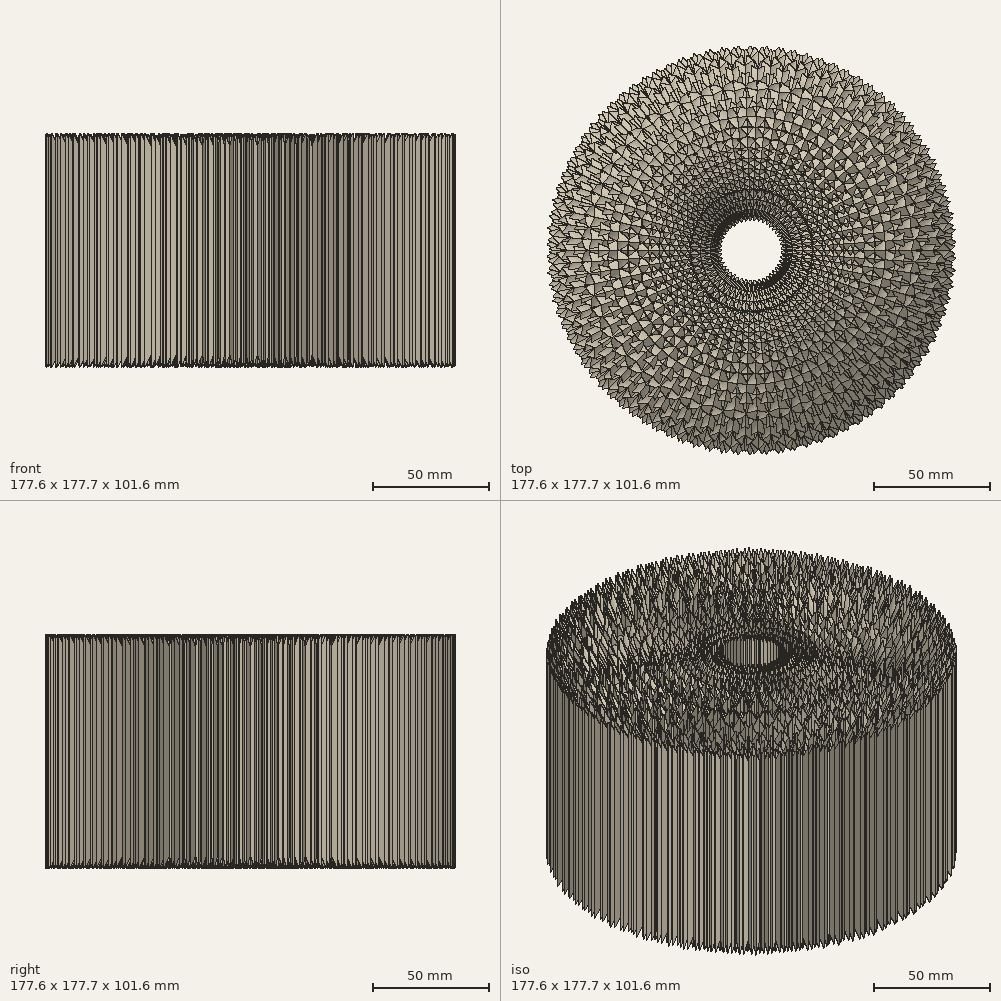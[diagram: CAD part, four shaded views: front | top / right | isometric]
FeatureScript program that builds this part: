
annotation { "Feature Type Name" : "Feature", "Feature Type Description" : "" }
export const myFeature = defineFeature(function(context is Context, id is Id, definition is map)
    precondition{}
    {
        {
            var Q0;
            Q0=qCreatedBy(makeId("Front.planeOp"),FACE);
            var sketch = newSketch(context, id + "F0", { "sketchPlane" : qUnion([Q0])});
            skLineSegment(sketch, "E0", {"start": v(0, -3.4) * mm, "end": v(0, 98.2) * mm});
            skLineSegment(sketch, "E1", {"start": v(-12.7, 0) * mm, "end": v(-12.7, 101.6) * mm});
            skArc(sketch, "E2", {"start": v(-12.7, 101.6) * mm, "mid": v(-26.31, 50.8) * mm, "end": v(-12.7, 0) * mm});
            skLineSegment(sketch, "E3", {"start": v(-50.8, 91.75) * mm, "end": v(-50.8, 14) * mm});
            skSolve(sketch);
        }
        {
            var Q0;
            Q0 = qSketchRegion(id + "F0", true);
            var Q1;
            Q1=sQuery(id+"F0.wireOp",EDGE,"E1");
            revolve(context, id + "F1", {"entities" : qUnion([Q0]), "axis" : qUnion([Q1]), "revolveType" : RevolveType.SYMMETRIC, "angle" : 60 * degree});
        }
        {
            var Q0;
            Q0=makeQuery(id+"F1.opRevolve","SWEPT_BODY",BODY,{"disambiguationData":[OSD([sQuery(id+"F0.wireOp",EDGE,"E1"),sQuery(id+"F0.wireOp",EDGE,"E2")])]});
            var Q1;
            Q1=sQuery(id+"F0.wireOp",EDGE,"E3");
            circularPattern(context, id + "F2", {"entities" : qUnion([Q0]), "axis" : qUnion([Q1]), "angle" : 360 * degree, "instanceCount" : 45, "equalSpace" : true, "computeTransformsWithoutBuiltin" : true});
        }
        {
            var Q0;
            Q0=makeQuery(id+"F2.opPattern","COPY",BODY,{"derivedFrom":makeQuery(id+"F1.opRevolve","SWEPT_BODY",BODY,{"disambiguationData":[OSD([sQuery(id+"F0.wireOp",EDGE,"E1"),sQuery(id+"F0.wireOp",EDGE,"E2")])]}),"instanceName":"5"});
            var Q1;
            Q1=makeQuery(id+"F2.opPattern","COPY",BODY,{"derivedFrom":makeQuery(id+"F1.opRevolve","SWEPT_BODY",BODY,{"disambiguationData":[OSD([sQuery(id+"F0.wireOp",EDGE,"E1"),sQuery(id+"F0.wireOp",EDGE,"E2")])]}),"instanceName":"2"});
            var Q2;
            Q2=makeQuery(id+"F2.opPattern","COPY",BODY,{"derivedFrom":makeQuery(id+"F1.opRevolve","SWEPT_BODY",BODY,{"disambiguationData":[OSD([sQuery(id+"F0.wireOp",EDGE,"E1"),sQuery(id+"F0.wireOp",EDGE,"E2")])]}),"instanceName":"1"});
            var Q3;
            Q3=makeQuery(id+"F2.opPattern","COPY",BODY,{"derivedFrom":makeQuery(id+"F1.opRevolve","SWEPT_BODY",BODY,{"disambiguationData":[OSD([sQuery(id+"F0.wireOp",EDGE,"E1"),sQuery(id+"F0.wireOp",EDGE,"E2")])]}),"instanceName":"7"});
            var Q4;
            Q4=makeQuery(id+"F2.opPattern","COPY",BODY,{"derivedFrom":makeQuery(id+"F1.opRevolve","SWEPT_BODY",BODY,{"disambiguationData":[OSD([sQuery(id+"F0.wireOp",EDGE,"E1"),sQuery(id+"F0.wireOp",EDGE,"E2")])]}),"instanceName":"6"});
            var Q5;
            Q5=makeQuery(id+"F2.opPattern","COPY",BODY,{"derivedFrom":makeQuery(id+"F1.opRevolve","SWEPT_BODY",BODY,{"disambiguationData":[OSD([sQuery(id+"F0.wireOp",EDGE,"E1"),sQuery(id+"F0.wireOp",EDGE,"E2")])]}),"instanceName":"10"});
            var Q6;
            Q6=makeQuery(id+"F2.opPattern","COPY",BODY,{"derivedFrom":makeQuery(id+"F1.opRevolve","SWEPT_BODY",BODY,{"disambiguationData":[OSD([sQuery(id+"F0.wireOp",EDGE,"E1"),sQuery(id+"F0.wireOp",EDGE,"E2")])]}),"instanceName":"3"});
            var Q7;
            Q7=makeQuery(id+"F2.opPattern","COPY",BODY,{"derivedFrom":makeQuery(id+"F1.opRevolve","SWEPT_BODY",BODY,{"disambiguationData":[OSD([sQuery(id+"F0.wireOp",EDGE,"E1"),sQuery(id+"F0.wireOp",EDGE,"E2")])]}),"instanceName":"4"});
            var Q8;
            Q8=makeQuery(id+"F2.opPattern","COPY",BODY,{"derivedFrom":makeQuery(id+"F1.opRevolve","SWEPT_BODY",BODY,{"disambiguationData":[OSD([sQuery(id+"F0.wireOp",EDGE,"E1"),sQuery(id+"F0.wireOp",EDGE,"E2")])]}),"instanceName":"9"});
            var Q9;
            Q9=makeQuery(id+"F2.opPattern","COPY",BODY,{"derivedFrom":makeQuery(id+"F1.opRevolve","SWEPT_BODY",BODY,{"disambiguationData":[OSD([sQuery(id+"F0.wireOp",EDGE,"E1"),sQuery(id+"F0.wireOp",EDGE,"E2")])]}),"instanceName":"8"});
            var Q10;
            Q10=makeQuery(id+"F1.opRevolve","SWEPT_BODY",BODY,{"disambiguationData":[OSD([sQuery(id+"F0.wireOp",EDGE,"E1"),sQuery(id+"F0.wireOp",EDGE,"E2")])]});
            var Q11;
            Q11=makeQuery(id+"F2.opPattern","COPY",BODY,{"derivedFrom":makeQuery(id+"F1.opRevolve","SWEPT_BODY",BODY,{"disambiguationData":[OSD([sQuery(id+"F0.wireOp",EDGE,"E1"),sQuery(id+"F0.wireOp",EDGE,"E2")])]}),"instanceName":"11"});
            var Q12;
            Q12=makeQuery(id+"F2.opPattern","COPY",BODY,{"derivedFrom":makeQuery(id+"F1.opRevolve","SWEPT_BODY",BODY,{"disambiguationData":[OSD([sQuery(id+"F0.wireOp",EDGE,"E1"),sQuery(id+"F0.wireOp",EDGE,"E2")])]}),"instanceName":"12"});
            var Q13;
            Q13=makeQuery(id+"F2.opPattern","COPY",BODY,{"derivedFrom":makeQuery(id+"F1.opRevolve","SWEPT_BODY",BODY,{"disambiguationData":[OSD([sQuery(id+"F0.wireOp",EDGE,"E1"),sQuery(id+"F0.wireOp",EDGE,"E2")])]}),"instanceName":"13"});
            var Q14;
            Q14=makeQuery(id+"F2.opPattern","COPY",BODY,{"derivedFrom":makeQuery(id+"F1.opRevolve","SWEPT_BODY",BODY,{"disambiguationData":[OSD([sQuery(id+"F0.wireOp",EDGE,"E1"),sQuery(id+"F0.wireOp",EDGE,"E2")])]}),"instanceName":"14"});
            var Q15;
            Q15=makeQuery(id+"F2.opPattern","COPY",BODY,{"derivedFrom":makeQuery(id+"F1.opRevolve","SWEPT_BODY",BODY,{"disambiguationData":[OSD([sQuery(id+"F0.wireOp",EDGE,"E1"),sQuery(id+"F0.wireOp",EDGE,"E2")])]}),"instanceName":"15"});
            var Q16;
            Q16=makeQuery(id+"F2.opPattern","COPY",BODY,{"derivedFrom":makeQuery(id+"F1.opRevolve","SWEPT_BODY",BODY,{"disambiguationData":[OSD([sQuery(id+"F0.wireOp",EDGE,"E1"),sQuery(id+"F0.wireOp",EDGE,"E2")])]}),"instanceName":"16"});
            var Q17;
            Q17=makeQuery(id+"F2.opPattern","COPY",BODY,{"derivedFrom":makeQuery(id+"F1.opRevolve","SWEPT_BODY",BODY,{"disambiguationData":[OSD([sQuery(id+"F0.wireOp",EDGE,"E1"),sQuery(id+"F0.wireOp",EDGE,"E2")])]}),"instanceName":"17"});
            var Q18;
            Q18=makeQuery(id+"F2.opPattern","COPY",BODY,{"derivedFrom":makeQuery(id+"F1.opRevolve","SWEPT_BODY",BODY,{"disambiguationData":[OSD([sQuery(id+"F0.wireOp",EDGE,"E1"),sQuery(id+"F0.wireOp",EDGE,"E2")])]}),"instanceName":"18"});
            var Q19;
            Q19=makeQuery(id+"F2.opPattern","COPY",BODY,{"derivedFrom":makeQuery(id+"F1.opRevolve","SWEPT_BODY",BODY,{"disambiguationData":[OSD([sQuery(id+"F0.wireOp",EDGE,"E1"),sQuery(id+"F0.wireOp",EDGE,"E2")])]}),"instanceName":"19"});
            var Q20;
            Q20=makeQuery(id+"F2.opPattern","COPY",BODY,{"derivedFrom":makeQuery(id+"F1.opRevolve","SWEPT_BODY",BODY,{"disambiguationData":[OSD([sQuery(id+"F0.wireOp",EDGE,"E1"),sQuery(id+"F0.wireOp",EDGE,"E2")])]}),"instanceName":"20"});
            var Q21;
            Q21=makeQuery(id+"F2.opPattern","COPY",BODY,{"derivedFrom":makeQuery(id+"F1.opRevolve","SWEPT_BODY",BODY,{"disambiguationData":[OSD([sQuery(id+"F0.wireOp",EDGE,"E1"),sQuery(id+"F0.wireOp",EDGE,"E2")])]}),"instanceName":"21"});
            var Q22;
            Q22=makeQuery(id+"F2.opPattern","COPY",BODY,{"derivedFrom":makeQuery(id+"F1.opRevolve","SWEPT_BODY",BODY,{"disambiguationData":[OSD([sQuery(id+"F0.wireOp",EDGE,"E1"),sQuery(id+"F0.wireOp",EDGE,"E2")])]}),"instanceName":"22"});
            var Q23;
            Q23=makeQuery(id+"F2.opPattern","COPY",BODY,{"derivedFrom":makeQuery(id+"F1.opRevolve","SWEPT_BODY",BODY,{"disambiguationData":[OSD([sQuery(id+"F0.wireOp",EDGE,"E1"),sQuery(id+"F0.wireOp",EDGE,"E2")])]}),"instanceName":"23"});
            var Q24;
            Q24=makeQuery(id+"F2.opPattern","COPY",BODY,{"derivedFrom":makeQuery(id+"F1.opRevolve","SWEPT_BODY",BODY,{"disambiguationData":[OSD([sQuery(id+"F0.wireOp",EDGE,"E1"),sQuery(id+"F0.wireOp",EDGE,"E2")])]}),"instanceName":"24"});
            var Q25;
            Q25=makeQuery(id+"F2.opPattern","COPY",BODY,{"derivedFrom":makeQuery(id+"F1.opRevolve","SWEPT_BODY",BODY,{"disambiguationData":[OSD([sQuery(id+"F0.wireOp",EDGE,"E1"),sQuery(id+"F0.wireOp",EDGE,"E2")])]}),"instanceName":"25"});
            var Q26;
            Q26=makeQuery(id+"F2.opPattern","COPY",BODY,{"derivedFrom":makeQuery(id+"F1.opRevolve","SWEPT_BODY",BODY,{"disambiguationData":[OSD([sQuery(id+"F0.wireOp",EDGE,"E1"),sQuery(id+"F0.wireOp",EDGE,"E2")])]}),"instanceName":"26"});
            var Q27;
            Q27=makeQuery(id+"F2.opPattern","COPY",BODY,{"derivedFrom":makeQuery(id+"F1.opRevolve","SWEPT_BODY",BODY,{"disambiguationData":[OSD([sQuery(id+"F0.wireOp",EDGE,"E1"),sQuery(id+"F0.wireOp",EDGE,"E2")])]}),"instanceName":"27"});
            var Q28;
            Q28=makeQuery(id+"F2.opPattern","COPY",BODY,{"derivedFrom":makeQuery(id+"F1.opRevolve","SWEPT_BODY",BODY,{"disambiguationData":[OSD([sQuery(id+"F0.wireOp",EDGE,"E1"),sQuery(id+"F0.wireOp",EDGE,"E2")])]}),"instanceName":"28"});
            var Q29;
            Q29=makeQuery(id+"F2.opPattern","COPY",BODY,{"derivedFrom":makeQuery(id+"F1.opRevolve","SWEPT_BODY",BODY,{"disambiguationData":[OSD([sQuery(id+"F0.wireOp",EDGE,"E1"),sQuery(id+"F0.wireOp",EDGE,"E2")])]}),"instanceName":"29"});
            var Q30;
            Q30=makeQuery(id+"F2.opPattern","COPY",BODY,{"derivedFrom":makeQuery(id+"F1.opRevolve","SWEPT_BODY",BODY,{"disambiguationData":[OSD([sQuery(id+"F0.wireOp",EDGE,"E1"),sQuery(id+"F0.wireOp",EDGE,"E2")])]}),"instanceName":"30"});
            var Q31;
            Q31=makeQuery(id+"F2.opPattern","COPY",BODY,{"derivedFrom":makeQuery(id+"F1.opRevolve","SWEPT_BODY",BODY,{"disambiguationData":[OSD([sQuery(id+"F0.wireOp",EDGE,"E1"),sQuery(id+"F0.wireOp",EDGE,"E2")])]}),"instanceName":"31"});
            var Q32;
            Q32=makeQuery(id+"F2.opPattern","COPY",BODY,{"derivedFrom":makeQuery(id+"F1.opRevolve","SWEPT_BODY",BODY,{"disambiguationData":[OSD([sQuery(id+"F0.wireOp",EDGE,"E1"),sQuery(id+"F0.wireOp",EDGE,"E2")])]}),"instanceName":"32"});
            var Q33;
            Q33=makeQuery(id+"F2.opPattern","COPY",BODY,{"derivedFrom":makeQuery(id+"F1.opRevolve","SWEPT_BODY",BODY,{"disambiguationData":[OSD([sQuery(id+"F0.wireOp",EDGE,"E1"),sQuery(id+"F0.wireOp",EDGE,"E2")])]}),"instanceName":"33"});
            var Q34;
            Q34=makeQuery(id+"F2.opPattern","COPY",BODY,{"derivedFrom":makeQuery(id+"F1.opRevolve","SWEPT_BODY",BODY,{"disambiguationData":[OSD([sQuery(id+"F0.wireOp",EDGE,"E1"),sQuery(id+"F0.wireOp",EDGE,"E2")])]}),"instanceName":"34"});
            var Q35;
            Q35=makeQuery(id+"F2.opPattern","COPY",BODY,{"derivedFrom":makeQuery(id+"F1.opRevolve","SWEPT_BODY",BODY,{"disambiguationData":[OSD([sQuery(id+"F0.wireOp",EDGE,"E1"),sQuery(id+"F0.wireOp",EDGE,"E2")])]}),"instanceName":"35"});
            var Q36;
            Q36=makeQuery(id+"F2.opPattern","COPY",BODY,{"derivedFrom":makeQuery(id+"F1.opRevolve","SWEPT_BODY",BODY,{"disambiguationData":[OSD([sQuery(id+"F0.wireOp",EDGE,"E1"),sQuery(id+"F0.wireOp",EDGE,"E2")])]}),"instanceName":"36"});
            var Q37;
            Q37=makeQuery(id+"F2.opPattern","COPY",BODY,{"derivedFrom":makeQuery(id+"F1.opRevolve","SWEPT_BODY",BODY,{"disambiguationData":[OSD([sQuery(id+"F0.wireOp",EDGE,"E1"),sQuery(id+"F0.wireOp",EDGE,"E2")])]}),"instanceName":"37"});
            var Q38;
            Q38=makeQuery(id+"F2.opPattern","COPY",BODY,{"derivedFrom":makeQuery(id+"F1.opRevolve","SWEPT_BODY",BODY,{"disambiguationData":[OSD([sQuery(id+"F0.wireOp",EDGE,"E1"),sQuery(id+"F0.wireOp",EDGE,"E2")])]}),"instanceName":"38"});
            var Q39;
            Q39=makeQuery(id+"F2.opPattern","COPY",BODY,{"derivedFrom":makeQuery(id+"F1.opRevolve","SWEPT_BODY",BODY,{"disambiguationData":[OSD([sQuery(id+"F0.wireOp",EDGE,"E1"),sQuery(id+"F0.wireOp",EDGE,"E2")])]}),"instanceName":"39"});
            var Q40;
            Q40=makeQuery(id+"F2.opPattern","COPY",BODY,{"derivedFrom":makeQuery(id+"F1.opRevolve","SWEPT_BODY",BODY,{"disambiguationData":[OSD([sQuery(id+"F0.wireOp",EDGE,"E1"),sQuery(id+"F0.wireOp",EDGE,"E2")])]}),"instanceName":"40"});
            var Q41;
            Q41=makeQuery(id+"F2.opPattern","COPY",BODY,{"derivedFrom":makeQuery(id+"F1.opRevolve","SWEPT_BODY",BODY,{"disambiguationData":[OSD([sQuery(id+"F0.wireOp",EDGE,"E1"),sQuery(id+"F0.wireOp",EDGE,"E2")])]}),"instanceName":"41"});
            var Q42;
            Q42=makeQuery(id+"F2.opPattern","COPY",BODY,{"derivedFrom":makeQuery(id+"F1.opRevolve","SWEPT_BODY",BODY,{"disambiguationData":[OSD([sQuery(id+"F0.wireOp",EDGE,"E1"),sQuery(id+"F0.wireOp",EDGE,"E2")])]}),"instanceName":"42"});
            var Q43;
            Q43=makeQuery(id+"F2.opPattern","COPY",BODY,{"derivedFrom":makeQuery(id+"F1.opRevolve","SWEPT_BODY",BODY,{"disambiguationData":[OSD([sQuery(id+"F0.wireOp",EDGE,"E1"),sQuery(id+"F0.wireOp",EDGE,"E2")])]}),"instanceName":"43"});
            var Q44;
            Q44=makeQuery(id+"F2.opPattern","COPY",BODY,{"derivedFrom":makeQuery(id+"F1.opRevolve","SWEPT_BODY",BODY,{"disambiguationData":[OSD([sQuery(id+"F0.wireOp",EDGE,"E1"),sQuery(id+"F0.wireOp",EDGE,"E2")])]}),"instanceName":"44"});
            var Q45;
            Q45=sQuery(id+"F0.wireOp",EDGE,"E0");
            circularPattern(context, id + "F3", {"entities" : qUnion([Q0, Q1, Q2, Q3, Q4, Q5, Q6, Q7, Q8, Q9, Q10, Q11, Q12, Q13, Q14, Q15, Q16, Q17, Q18, Q19, Q20, Q21, Q22, Q23, Q24, Q25, Q26, Q27, Q28, Q29, Q30, Q31, Q32, Q33, Q34, Q35, Q36, Q37, Q38, Q39, Q40, Q41, Q42, Q43, Q44]), "axis" : qUnion([Q45]), "angle" : 360 * degree, "instanceCount" : 45, "equalSpace" : true, "computeTransformsWithoutBuiltin" : true});
        }
    });
